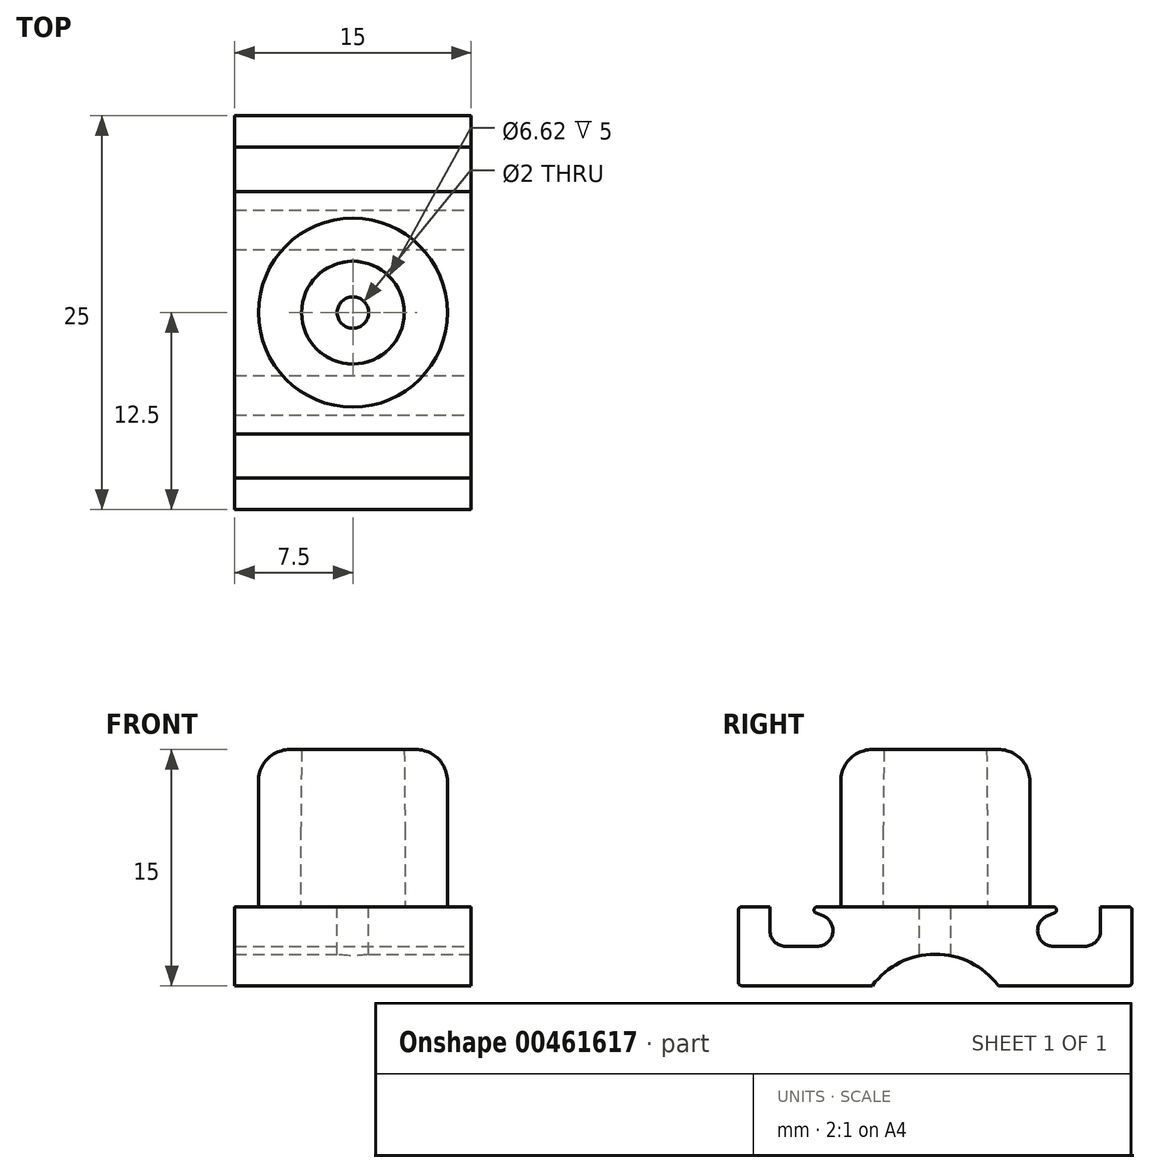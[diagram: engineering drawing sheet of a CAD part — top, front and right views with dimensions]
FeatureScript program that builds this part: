
annotation { "Feature Type Name" : "Feature", "Feature Type Description" : "" }
export const myFeature = defineFeature(function(context is Context, id is Id, definition is map)
    precondition{}
    {
        {
            var Q0;
            Q0=qCreatedBy(makeId("Right.planeOp"),FACE);
            var sketch = newSketch(context, id + "F0", { "sketchPlane" : qUnion([Q0])});
            skLineSegment(sketch, "E0", {"start": v(-3.31, 0) * mm, "end": v(-3.31, 5) * mm});
            skLineSegment(sketch, "E1", {"start": v(-3.3, 5) * mm, "end": v(-3.26, 10) * mm});
            skLineSegment(sketch, "E2", {"start": v(-3.26, 10) * mm, "end": v(-6, 10) * mm});
            skLineSegment(sketch, "E3", {"start": v(-6, 10) * mm, "end": v(-6, 0) * mm});
            skLineSegment(sketch, "E4", {"start": v(-6, 0) * mm, "end": v(-3.31, 0) * mm});
            skLineSegment(sketch, "E5", {"start": v(0, 0) * mm, "end": v(0, 56.82) * mm, "construction": true});
            skSolve(sketch);
        }
        {
            var Q0;
            Q0 = qSketchRegion(id + "F0", true);
            var Q1;
            Q1=sQuery(id+"F0.wireOp",EDGE,"E5");
            revolve(context, id + "F1", {"entities" : qUnion([Q0]), "axis" : qUnion([Q1]), "revolveType" : RevolveType.FULL});
        }
        {
            var Q0;
            Q0=makeQuery(id+"F1.opRevolve","SWEPT_EDGE",EDGE,{"disambiguationData":[OSD([sQuery(id+"F0.wireOp",EDGE,"E2"),sQuery(id+"F0.wireOp",EDGE,"E3")])]});
            fillet(context, id + "F2", {"entities" : qUnion([Q0]), "radius" : 2 * mm, "tangentPropagation" : true, "allowEdgeOverflow" : false});
        }
        {
            var Q0;
            Q0=qCreatedBy(makeId("Right.planeOp"),FACE);
            var sketch = newSketch(context, id + "F3", { "sketchPlane" : qUnion([Q0])});
            skLineSegment(sketch, "E6.bottom", {"start": v(-12.5, 0) * mm, "end": v(12.5, 0) * mm});
            skLineSegment(sketch, "E6.top", {"start": v(-12.5, -5) * mm, "end": v(12.5, -5) * mm});
            skLineSegment(sketch, "E6.left", {"start": v(-12.5, 0) * mm, "end": v(-12.5, -5) * mm});
            skLineSegment(sketch, "E6.right", {"start": v(12.5, 0) * mm, "end": v(12.5, -5) * mm});
            skLineSegment(sketch, "E7", {"start": v(0, 0) * mm, "end": v(0, -15.84) * mm, "construction": true});
            skPoint(sketch, "E7.endSnap0", {"position": v(0, 0) * mm});
            skSolve(sketch);
        }
        {
            var Q0;
            Q0 = qSketchRegion(id + "F3", true);
            extrude(context, id + "F4", {"entities" : qUnion([Q0]), "operationType" : NewBodyOperationType.ADD, "endBound" : BoundingType.SYMMETRIC, "depth" : 15 * mm});
        }
        {
            var Q0;
            Q0=qCreatedBy(makeId("Right.planeOp"),FACE);
            var sketch = newSketch(context, id + "F5", { "sketchPlane" : qUnion([Q0])});
            skLineSegment(sketch, "E8", {"start": v(0, 0) * mm, "end": v(0, -34.8) * mm, "construction": true});
            skLineSegment(sketch, "E9", {"start": v(-10.5, 0) * mm, "end": v(-10.5, -1.5) * mm});
            skLineSegment(sketch, "E10", {"start": v(-9.5, -2.5) * mm, "end": v(-7.5, -2.5) * mm});
            skArc(sketch, "E11", {"start": v(-7.5, -2.5) * mm, "mid": v(-6.52, -1.7) * mm, "end": v(-7.12, -0.58) * mm});
            skLineSegment(sketch, "E12", {"start": v(-7.12, -0.58) * mm, "end": v(-8.5, 0) * mm});
            skLineSegment(sketch, "E13", {"start": v(-8.5, 0) * mm, "end": v(-10.5, 0) * mm});
            skPoint(sketch, "E14.visualSharp", {"position": v(-10.5, -2.5) * mm});
            skArc(sketch, "E14.filletArc", {"start": v(-10.5, -1.5) * mm, "mid": v(-10.2, -2.2) * mm, "end": v(-9.5, -2.5) * mm});
            skLineSegment(sketch, "E15.MirrorCS", {"start": v(8.5, 0) * mm, "end": v(10.5, 0) * mm});
            skLineSegment(sketch, "E16.MirrorCS", {"start": v(7.12, -0.58) * mm, "end": v(8.5, 0) * mm});
            skArc(sketch, "E17.MirrorCS", {"start": v(7.5, -2.5) * mm, "mid": v(6.52, -1.7) * mm, "end": v(7.12, -0.58) * mm});
            skLineSegment(sketch, "E18.MirrorCS", {"start": v(9.5, -2.5) * mm, "end": v(7.5, -2.5) * mm});
            skArc(sketch, "E19.MirrorCS", {"start": v(10.5, -1.5) * mm, "mid": v(10.2, -2.2) * mm, "end": v(9.5, -2.5) * mm});
            skLineSegment(sketch, "E20.MirrorCS", {"start": v(10.5, 0) * mm, "end": v(10.5, -1.5) * mm});
            skSolve(sketch);
        }
        {
            var Q0;
            Q0 = qSketchRegion(id + "F5", true);
            extrude(context, id + "F6", {"entities" : qUnion([Q0]), "operationType" : NewBodyOperationType.REMOVE, "endBound" : BoundingType.SYMMETRIC, "oppositeDirection" : true, "depth" : 25 * mm});
        }
        {
            var Q0;
            Q0=makeQuery(id+"F6.boolean.opBoolean","COPY",EDGE,{"derivedFrom":makeQuery(id+"F6.opExtrude","SWEPT_EDGE",EDGE,{"disambiguationData":[OSD([sQuery(id+"F5.wireOp",EDGE,"E12"),sQuery(id+"F5.wireOp",EDGE,"E13")])]})});
            var Q1;
            Q1=makeQuery(id+"F6.boolean.opBoolean","COPY",EDGE,{"derivedFrom":makeQuery(id+"F6.opExtrude","SWEPT_EDGE",EDGE,{"disambiguationData":[OSD([sQuery(id+"F5.wireOp",EDGE,"E15.MirrorCS"),sQuery(id+"F5.wireOp",EDGE,"E16.MirrorCS")])]})});
            var Q2;
            Q2=makeQuery(id+"F4.opExtrude","SWEPT_EDGE",EDGE,{"disambiguationData":[OSD([sQuery(id+"F3.wireOp",EDGE,"E6.bottom"),sQuery(id+"F3.wireOp",EDGE,"E6.left")])]});
            var Q3;
            Q3=makeQuery(id+"F4.opExtrude","SWEPT_EDGE",EDGE,{"disambiguationData":[OSD([sQuery(id+"F3.wireOp",EDGE,"E6.bottom"),sQuery(id+"F3.wireOp",EDGE,"E6.right")])]});
            var Q4;
            Q4=makeQuery(id+"F4.opExtrude","SWEPT_EDGE",EDGE,{"disambiguationData":[OSD([sQuery(id+"F3.wireOp",EDGE,"E6.top"),sQuery(id+"F3.wireOp",EDGE,"E6.left")])]});
            var Q5;
            Q5=makeQuery(id+"F4.opExtrude","SWEPT_EDGE",EDGE,{"disambiguationData":[OSD([sQuery(id+"F3.wireOp",EDGE,"E6.top"),sQuery(id+"F3.wireOp",EDGE,"E6.right")])]});
            fillet(context, id + "F7", {"entities" : qUnion([Q0, Q1, Q2, Q3, Q4, Q5]), "radius" : 0.2 * mm, "tangentPropagation" : true, "allowEdgeOverflow" : false});
        }
        {
            var Q0;
            Q0=qCreatedBy(makeId("Right.planeOp"),FACE);
            var sketch = newSketch(context, id + "F8", { "sketchPlane" : qUnion([Q0])});
            skArc(sketch, "E21", {"start": v(4, -5) * mm, "mid": v(0, -3) * mm, "end": v(-4, -5) * mm});
            skLineSegment(sketch, "E22", {"start": v(-4, -5) * mm, "end": v(4, -5) * mm});
            skSolve(sketch);
        }
        {
            var Q0;
            Q0 = qSketchRegion(id + "F8", true);
            extrude(context, id + "F9", {"entities" : qUnion([Q0]), "operationType" : NewBodyOperationType.REMOVE, "endBound" : BoundingType.SYMMETRIC, "oppositeDirection" : true, "depth" : 25 * mm});
        }
        {
            var Q0;
            Q0=makeQuery(id+"F4.boolean.opBoolean","SPLIT",FACE,{"disambiguationData":[TD([makeQuery(id+"F1.opRevolve","SWEPT_FACE",FACE,{"disambiguationData":[OSD([sQuery(id+"F0.wireOp",EDGE,"E0")])]})])],"derivedFrom":makeQuery(id+"F4.opExtrude","SWEPT_FACE",FACE,{"disambiguationData":[OSD([sQuery(id+"F3.wireOp",EDGE,"E6.bottom")])]})});
            var sketch = newSketch(context, id + "F10", { "sketchPlane" : qUnion([Q0])});
            skCircle(sketch, "E23", {"center": v(0, 0) * mm, "radius": 1 * mm});
            skSolve(sketch);
        }
        {
            var Q0;
            Q0 = qSketchRegion(id + "F10", true);
            extrude(context, id + "F11", {"entities" : qUnion([Q0]), "operationType" : NewBodyOperationType.REMOVE, "endBound" : BoundingType.THROUGH_ALL, "oppositeDirection" : true, "depth" : 25 * mm});
        }
    });
